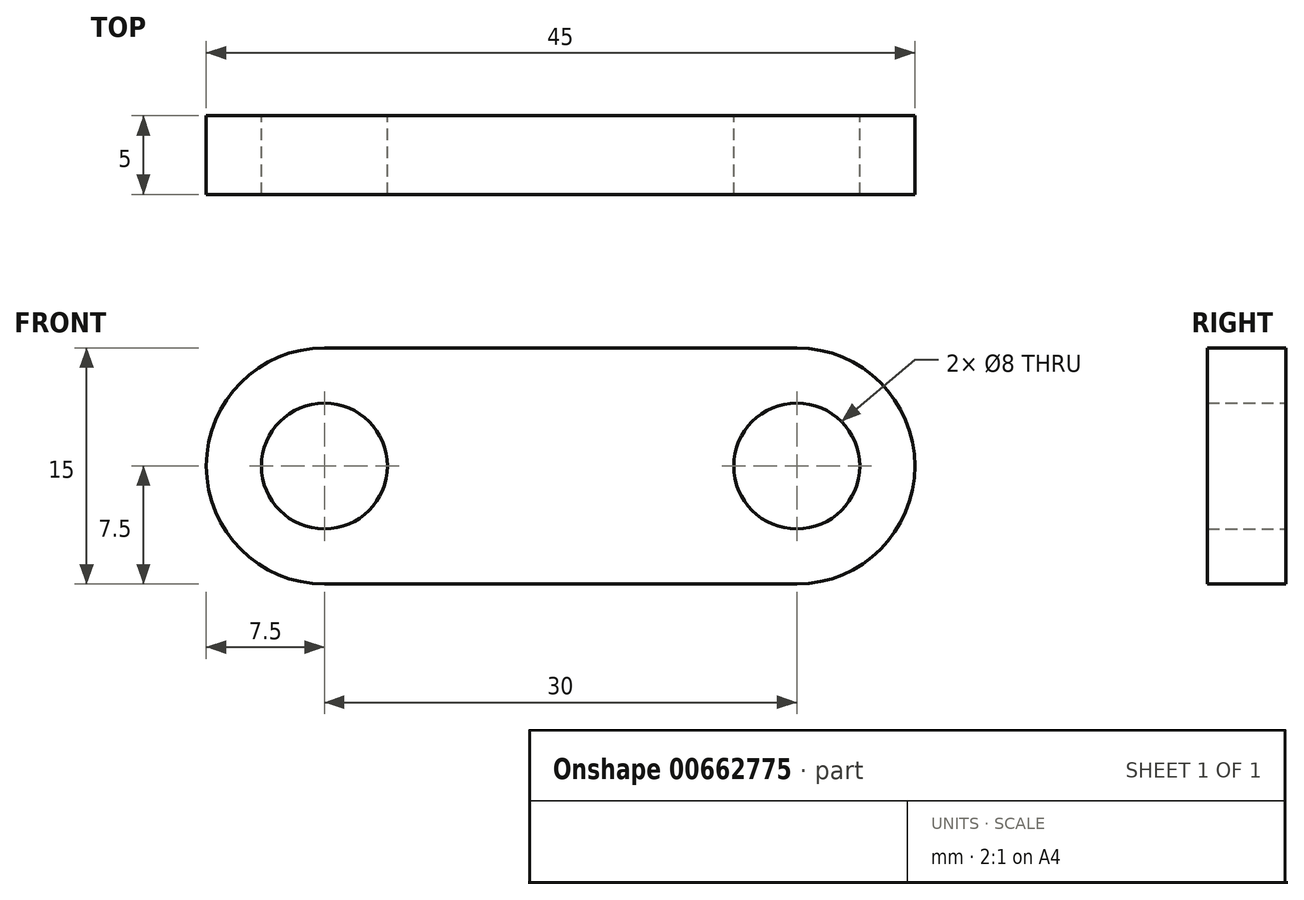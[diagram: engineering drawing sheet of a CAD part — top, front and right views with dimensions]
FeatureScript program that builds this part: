
annotation { "Feature Type Name" : "Feature", "Feature Type Description" : "" }
export const myFeature = defineFeature(function(context is Context, id is Id, definition is map)
    precondition{}
    {
        {
            var Q0;
            Q0=qCreatedBy(makeId("Front.planeOp"),FACE);
            var sketch = newSketch(context, id + "F0", { "sketchPlane" : qUnion([Q0])});
            skArc(sketch, "E0", {"start": v(0, 7.5) * mm, "mid": v(-7.5, 0) * mm, "end": v(0, -7.5) * mm});
            skArc(sketch, "E1", {"start": v(30, -7.5) * mm, "mid": v(37.5, 0) * mm, "end": v(30, 7.5) * mm});
            skCircle(sketch, "E2", {"center": v(0, 0) * mm, "radius": 4 * mm});
            skCircle(sketch, "E3", {"center": v(30, 0) * mm, "radius": 4 * mm});
            skLineSegment(sketch, "E4", {"start": v(0, 7.5) * mm, "end": v(30, 7.5) * mm});
            skLineSegment(sketch, "E5", {"start": v(0, -7.5) * mm, "end": v(30, -7.5) * mm});
            skSolve(sketch);
        }
        {
            var Q0;
            Q0 = qSketchRegion(id + "F0", true);
            extrude(context, id + "F1", {"entities" : qUnion([Q0]), "depth" : 5 * mm, "offsetDistance" : 25 * mm});
        }
    });
